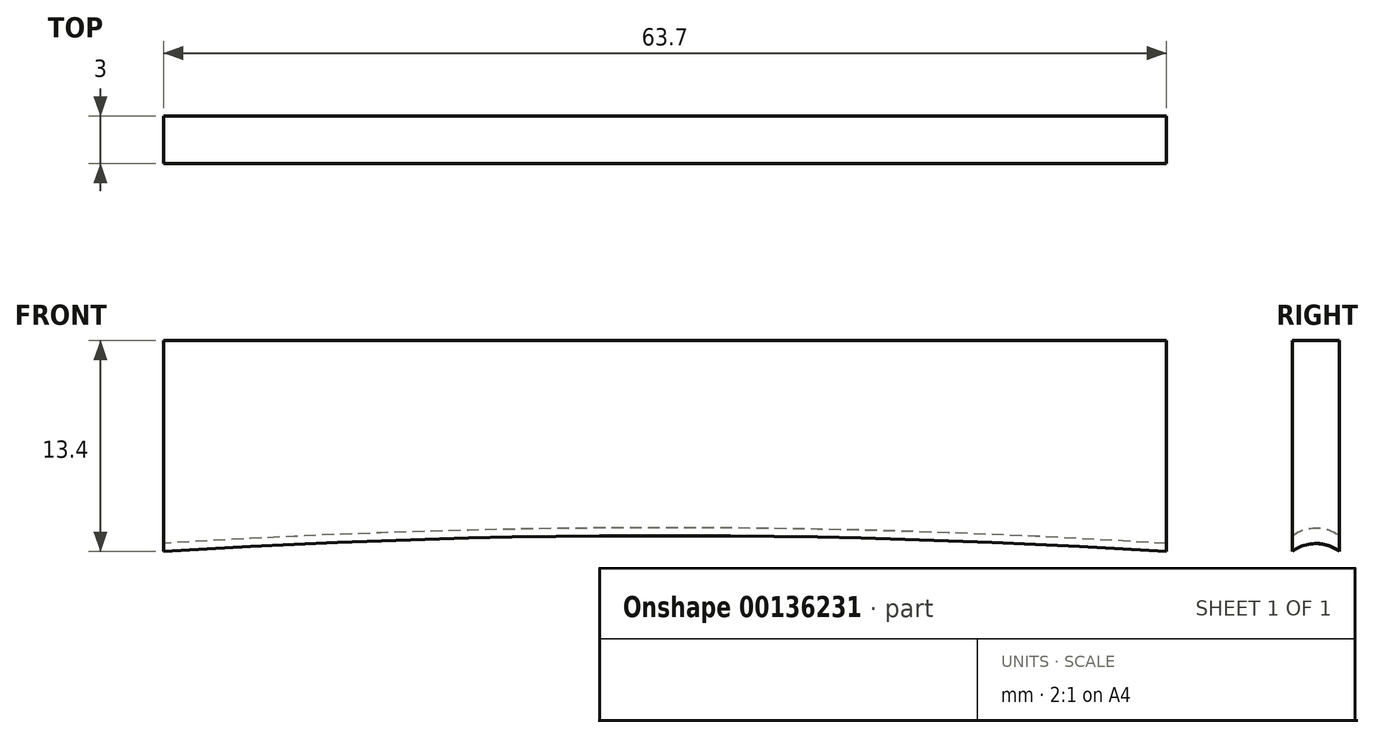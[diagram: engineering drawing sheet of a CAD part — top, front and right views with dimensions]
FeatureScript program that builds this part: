
annotation { "Feature Type Name" : "Feature", "Feature Type Description" : "" }
export const myFeature = defineFeature(function(context is Context, id is Id, definition is map)
    precondition{}
    {
        {
            var Q0;
            Q0=qCreatedBy(makeId("Front.planeOp"),FACE);
            var sketch = newSketch(context, id + "F0", { "sketchPlane" : qUnion([Q0])});
            skLineSegment(sketch, "E0.top", {"start": v(0, 13.4) * mm, "end": v(63.7, 13.4) * mm});
            skLineSegment(sketch, "E0.left", {"start": v(0, 0) * mm, "end": v(0, 13.4) * mm});
            skLineSegment(sketch, "E0.right", {"start": v(63.7, 0) * mm, "end": v(63.7, 13.4) * mm});
            skArc(sketch, "E1", {"start": v(0, 0) * mm, "mid": v(31.85, 1) * mm, "end": v(63.7, 0) * mm});
            skSolve(sketch);
        }
        {
            var Q0;
            Q0 = qSketchRegion(id + "F0", true);
            extrude(context, id + "F1", {"entities" : qUnion([Q0]), "depth" : 3 * mm});
        }
        {
            var Q0;
            Q0=makeQuery(id+"F1.opExtrude","SWEPT_FACE",FACE,{"disambiguationData":[OSD([sQuery(id+"F0.wireOp",EDGE,"E0.right")])]});
            var sketch = newSketch(context, id + "F2", { "sketchPlane" : qUnion([Q0])});
            skArc(sketch, "E2", {"start": v(0, 0) * mm, "mid": v(-1.5, 0.5) * mm, "end": v(-3, 0) * mm});
            skSolve(sketch);
        }
        {
            var Q0;
            Q0=makeQuery(id+"F2.imprint","IMPRINT",FACE,{"disambiguationData":[TD([[makeQuery(id+"F2.imprint","IMPRINT",EDGE,{"derivedFrom":sQuery(id+"F2.wireOp",EDGE,"E2")}),1.0]])]});
            var Q1;
            Q1=makeQuery(id+"F1.opExtrude","CAP_EDGE",EDGE,{"disambiguationData":[OSD([sQuery(id+"F0.wireOp",EDGE,"E1")])],"isStart":false});
            sweep(context, id + "F3", {"operationType" : NewBodyOperationType.REMOVE, "profiles" : qUnion([Q0]), "path" : qUnion([Q1])});
        }
    });
